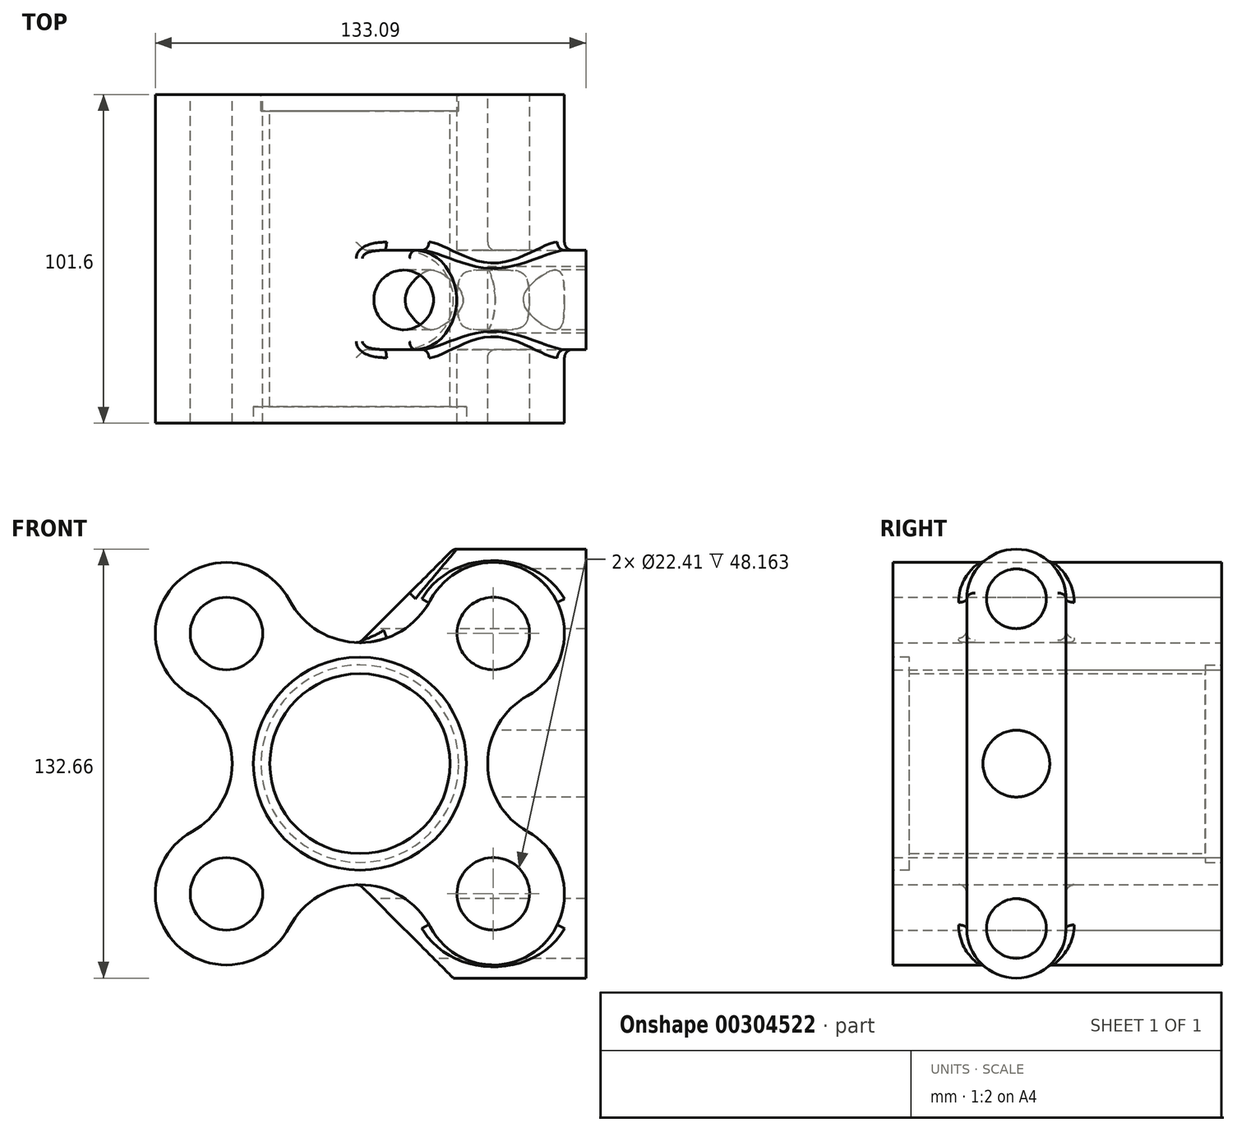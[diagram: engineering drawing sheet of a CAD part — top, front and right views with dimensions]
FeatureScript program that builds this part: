
annotation { "Feature Type Name" : "Feature", "Feature Type Description" : "" }
export const myFeature = defineFeature(function(context is Context, id is Id, definition is map)
    precondition{}
    {
        {
            var Q0;
            Q0=qCreatedBy(makeId("Front.planeOp"),FACE);
            var sketch = newSketch(context, id + "F0", { "sketchPlane" : qUnion([Q0])});
            skCircle(sketch, "E0", {"center": v(-41.24, 40.26) * mm, "radius": 11.2 * mm});
            skCircle(sketch, "E1.MirrorC", {"center": v(41.24, 40.26) * mm, "radius": 11.2 * mm});
            skCircle(sketch, "E2.MirrorC", {"center": v(-41.24, -40.26) * mm, "radius": 11.2 * mm});
            skCircle(sketch, "E3.MirrorC", {"center": v(41.24, -40.26) * mm, "radius": 11.2 * mm});
            skCircle(sketch, "E4", {"center": v(0, 0) * mm, "radius": 27.83 * mm});
            skArc(sketch, "E5", {"start": v(-21.8, 50.56) * mm, "mid": v(-56.66, 55.95) * mm, "end": v(-51.88, 21.01) * mm});
            skArc(sketch, "E6.MirrorC", {"start": v(-21.8, -50.56) * mm, "mid": v(-56.66, -55.95) * mm, "end": v(-51.88, -21.01) * mm});
            skArc(sketch, "E7.MirrorC", {"start": v(21.8, 50.56) * mm, "mid": v(56.66, 55.95) * mm, "end": v(51.88, 21.01) * mm});
            skArc(sketch, "E8.MirrorC", {"start": v(21.8, -50.56) * mm, "mid": v(56.66, -55.95) * mm, "end": v(51.88, -21.01) * mm});
            skArc(sketch, "E9", {"start": v(-51.88, -21.01) * mm, "mid": v(-39.5, 0) * mm, "end": v(-51.88, 21.01) * mm});
            skArc(sketch, "E10.MirrorC", {"start": v(51.88, -21.01) * mm, "mid": v(39.5, 0) * mm, "end": v(51.88, 21.01) * mm});
            skArc(sketch, "E11", {"start": v(-21.8, 50.56) * mm, "mid": v(0, 37.44) * mm, "end": v(21.8, 50.56) * mm});
            skArc(sketch, "E12.MirrorC", {"start": v(-21.8, -50.56) * mm, "mid": v(0, -37.44) * mm, "end": v(21.8, -50.56) * mm});
            skCircle(sketch, "E13", {"center": v(0, 0) * mm, "radius": 21.8 * mm});
            skPoint(sketch, "E14", {"position": v(0, 37.44) * mm});
            skSolve(sketch);
        }
        {
            var Q0;
            Q0=qCreatedBy(makeId("Right.planeOp"),FACE);
            var sketch = newSketch(context, id + "F1", { "sketchPlane" : qUnion([Q0])});
            skLineSegment(sketch, "E15.bottom", {"start": v(-15.34, 51) * mm, "end": v(15.34, 51) * mm});
            skLineSegment(sketch, "E15.top", {"start": v(-15.34, -51) * mm, "end": v(15.34, -51) * mm});
            skLineSegment(sketch, "E15.left", {"start": v(-15.34, 51) * mm, "end": v(-15.34, -51) * mm});
            skLineSegment(sketch, "E15.right", {"start": v(15.34, 51) * mm, "end": v(15.34, -51) * mm});
            skPoint(sketch, "E15.middle", {"position": v(0, 0) * mm});
            skArc(sketch, "E16", {"start": v(15.34, 51) * mm, "mid": v(0, 66.33) * mm, "end": v(-15.34, 51) * mm});
            skArc(sketch, "E17.MirrorCS", {"start": v(15.34, -51) * mm, "mid": v(0, -66.33) * mm, "end": v(-15.34, -51) * mm});
            skCircle(sketch, "E18", {"center": v(0, 51) * mm, "radius": 9.23 * mm});
            skCircle(sketch, "E19", {"center": v(0, 0) * mm, "radius": 10.32 * mm});
            skCircle(sketch, "E20.MirrorC", {"center": v(0, -51) * mm, "radius": 9.23 * mm});
            skSolve(sketch);
        }
        {
            var Q0;
            Q0=makeQuery(id+"F0.imprint","IMPRINT",FACE,{"disambiguationData":[TD([[makeQuery(id+"F0.imprint","IMPRINT",EDGE,{"derivedFrom":sQuery(id+"F0.wireOp",EDGE,"E0")}),-1.0]])]});
            extrude(context, id + "F2", {"entities" : qUnion([Q0]), "endBound" : BoundingType.SYMMETRIC, "depth" : 76.2 * mm});
        }
        {
            var Q0;
            Q0 = qSketchRegion(id + "F1", true);
            extrude(context, id + "F3", {"entities" : qUnion([Q0]), "operationType" : NewBodyOperationType.ADD, "depth" : 69.85 * mm});
        }
        {
            var Q0;
            Q0=makeQuery(id+"F2.opExtrude","CAP_FACE",FACE,{"disambiguationData":[OSD([sQuery(id+"F0.wireOp",EDGE,"E0"),sQuery(id+"F0.wireOp",EDGE,"E1.MirrorC"),sQuery(id+"F0.wireOp",EDGE,"E2.MirrorC"),sQuery(id+"F0.wireOp",EDGE,"E4"),sQuery(id+"F0.wireOp",EDGE,"E5"),sQuery(id+"F0.wireOp",EDGE,"E6.MirrorC"),sQuery(id+"F0.wireOp",EDGE,"E3.MirrorC"),sQuery(id+"F0.wireOp",EDGE,"E7.MirrorC"),sQuery(id+"F0.wireOp",EDGE,"E8.MirrorC"),sQuery(id+"F0.wireOp",EDGE,"E9"),sQuery(id+"F0.wireOp",EDGE,"E10.MirrorC"),sQuery(id+"F0.wireOp",EDGE,"E11"),sQuery(id+"F0.wireOp",EDGE,"E12.MirrorC")])],"isStart":false});
            var sketch = newSketch(context, id + "F4", { "sketchPlane" : qUnion([Q0])});
            skLineSegment(sketch, "E21.0", {"start": v(0, 51) * mm, "end": v(0, 66.33) * mm});
            skLineSegment(sketch, "E21.1", {"start": v(69.85, 51) * mm, "end": v(69.85, 66.33) * mm});
            skLineSegment(sketch, "E21.2", {"start": v(69.85, 51) * mm, "end": v(69.85, -51) * mm});
            skLineSegment(sketch, "E21.3", {"start": v(69.85, -51) * mm, "end": v(69.85, -66.33) * mm});
            skLineSegment(sketch, "E21.4", {"start": v(0, -51) * mm, "end": v(0, -66.33) * mm});
            skLineSegment(sketch, "E21.5", {"start": v(0, -37.44) * mm, "end": v(0, -51) * mm});
            skLineSegment(sketch, "E21.6", {"start": v(0, 51) * mm, "end": v(0, 37.44) * mm});
            skLineSegment(sketch, "E22", {"start": v(0, 66.33) * mm, "end": v(69.85, 66.33) * mm});
            skLineSegment(sketch, "E23", {"start": v(69.85, -66.33) * mm, "end": v(0, -66.33) * mm});
            skLineSegment(sketch, "E24", {"start": v(0, 37.44) * mm, "end": v(28.9, 66.33) * mm});
            skLineSegment(sketch, "E25", {"start": v(0, -37.44) * mm, "end": v(28.9, -66.33) * mm});
            skSolve(sketch);
        }
        {
            var Q0;
            Q0 = qSketchRegion(id + "F4", true);
            extrude(context, id + "F5", {"entities" : qUnion([Q0]), "operationType" : NewBodyOperationType.REMOVE, "endBound" : BoundingType.THROUGH_ALL, "oppositeDirection" : true, "depth" : 25.4 * mm});
        }
        {
            var Q0;
            {var subQ0=sQuery(id+"F1.wireOp",EDGE,"E15.left");Q0=makeQuery(id+"F3.boolean.opBoolean","SPLIT",FACE,{"disambiguationData":[TD([makeQuery(id+"F2.opExtrude","SWEPT_FACE",FACE,{"disambiguationData":[OSD([sQuery(id+"F0.wireOp",EDGE,"E4")])]})])],"derivedFrom":makeQuery(id+"F3.opExtrude","SWEPT_FACE",FACE,{"disambiguationData":[OSD([subQ0])]})});}
            extrude(context, id + "F6", {"entities" : qUnion([Q0]), "operationType" : NewBodyOperationType.REMOVE, "endBound" : BoundingType.THROUGH_ALL, "oppositeDirection" : true, "depth" : 25.4 * mm});
        }
        {
            var Q0;
            Q0=makeQuery(id+"F2.opExtrude","CAP_FACE",FACE,{"disambiguationData":[OSD([sQuery(id+"F0.wireOp",EDGE,"E0"),sQuery(id+"F0.wireOp",EDGE,"E1.MirrorC"),sQuery(id+"F0.wireOp",EDGE,"E2.MirrorC"),sQuery(id+"F0.wireOp",EDGE,"E4"),sQuery(id+"F0.wireOp",EDGE,"E5"),sQuery(id+"F0.wireOp",EDGE,"E6.MirrorC"),sQuery(id+"F0.wireOp",EDGE,"E3.MirrorC"),sQuery(id+"F0.wireOp",EDGE,"E7.MirrorC"),sQuery(id+"F0.wireOp",EDGE,"E8.MirrorC"),sQuery(id+"F0.wireOp",EDGE,"E9"),sQuery(id+"F0.wireOp",EDGE,"E10.MirrorC"),sQuery(id+"F0.wireOp",EDGE,"E11"),sQuery(id+"F0.wireOp",EDGE,"E12.MirrorC")])],"isStart":false});
            var sketch = newSketch(context, id + "F7", { "sketchPlane" : qUnion([Q0])});
            skCircle(sketch, "E26", {"center": v(0, 0) * mm, "radius": 32.92 * mm});
            skSolve(sketch);
        }
        {
            var Q0;
            Q0=makeQuery(id+"F7.imprint","IMPRINT",FACE,{"disambiguationData":[TD([[makeQuery(id+"F7.imprint","IMPRINT",EDGE,{"derivedFrom":sQuery(id+"F7.wireOp",EDGE,"E26")}),1.0]])]});
            var Q1;
            Q1=sQuery(id+"F7.wireOp",EDGE,"E26");
            extrude(context, id + "F8", {"entities" : qUnion([Q0]), "operationType" : NewBodyOperationType.REMOVE, "surfaceEntities" : qUnion([Q1]), "oppositeDirection" : true, "depth" : 5.08 * mm});
        }
        {
            var Q0;
            {var subQ1=sQuery(id+"F1.wireOp",EDGE,"E15.left");Q0=makeQuery(id+"F5.boolean.opBoolean","INTERSECT",EDGE,{"derivedFrom":[makeQuery(id+"F3.boolean.opBoolean","SPLIT",FACE,{"disambiguationData":[TD([makeQuery(id+"F2.opExtrude","SWEPT_FACE",FACE,{"disambiguationData":[OSD([sQuery(id+"F0.wireOp",EDGE,"E11")])]})])],"derivedFrom":makeQuery(id+"F3.opExtrude","SWEPT_FACE",FACE,{"disambiguationData":[OSD([subQ1])]})}),makeQuery(id+"F5.opExtrude","SWEPT_FACE",FACE,{"disambiguationData":[OSD([sQuery(id+"F4.wireOp",EDGE,"E24")])]})]});}
            var Q1;
            Q1=makeQuery(id+"F3.boolean.opBoolean","INTERSECT",EDGE,{"derivedFrom":[makeQuery(id+"F2.opExtrude","SWEPT_FACE",FACE,{"disambiguationData":[OSD([sQuery(id+"F0.wireOp",EDGE,"E11")])]}),makeQuery(id+"F3.opExtrude","SWEPT_FACE",FACE,{"disambiguationData":[OSD([sQuery(id+"F1.wireOp",EDGE,"E15.left")])]})]});
            var Q2;
            Q2=makeQuery(id+"F3.boolean.opBoolean","INTERSECT",EDGE,{"disambiguationData":[OD(1.0)],"derivedFrom":[makeQuery(id+"F2.opExtrude","SWEPT_FACE",FACE,{"disambiguationData":[OSD([sQuery(id+"F0.wireOp",EDGE,"E7.MirrorC")])]}),makeQuery(id+"F3.opExtrude","SWEPT_FACE",FACE,{"disambiguationData":[OSD([sQuery(id+"F1.wireOp",EDGE,"E16")])]})]});
            var Q3;
            {var subQ0=sQuery(id+"F0.wireOp",EDGE,"E11");Q3=makeQuery(id+"F5.boolean.opBoolean","MERGE",EDGE,{"derivedFrom":[makeQuery(id+"F3.boolean.opBoolean","INTERSECT",EDGE,{"derivedFrom":[makeQuery(id+"F2.opExtrude","SWEPT_FACE",FACE,{"disambiguationData":[OSD([subQ0])]}),makeQuery(id+"F3.opExtrude","CAP_FACE",FACE,{"disambiguationData":[OSD([sQuery(id+"F1.wireOp",EDGE,"E15.left"),sQuery(id+"F1.wireOp",EDGE,"E15.right"),sQuery(id+"F1.wireOp",EDGE,"E16"),sQuery(id+"F1.wireOp",EDGE,"E17.MirrorCS"),sQuery(id+"F1.wireOp",EDGE,"E18"),sQuery(id+"F1.wireOp",EDGE,"E19"),sQuery(id+"F1.wireOp",EDGE,"E20.MirrorC")])],"isStart":true})]}),makeQuery(id+"F5.opExtrude","SWEPT_EDGE",EDGE,{"disambiguationData":[OSD([subQ0,sQuery(id+"F4.wireOp",EDGE,"E21.6"),sQuery(id+"F4.wireOp",EDGE,"E24")])]})]});}
            fillet(context, id + "F9", {"entities" : qUnion([Q0, Q1, Q2, Q3]), "radius" : 2.54 * mm, "tangentPropagation" : true, "allowEdgeOverflow" : false});
        }
        {
            var Q0;
            {var subQ0=sQuery(id+"F0.wireOp",EDGE,"E12.MirrorC");Q0=makeQuery(id+"F5.boolean.opBoolean","MERGE",EDGE,{"derivedFrom":[makeQuery(id+"F3.boolean.opBoolean","INTERSECT",EDGE,{"derivedFrom":[makeQuery(id+"F2.opExtrude","SWEPT_FACE",FACE,{"disambiguationData":[OSD([subQ0])]}),makeQuery(id+"F3.opExtrude","CAP_FACE",FACE,{"disambiguationData":[OSD([sQuery(id+"F1.wireOp",EDGE,"E15.left"),sQuery(id+"F1.wireOp",EDGE,"E15.right"),sQuery(id+"F1.wireOp",EDGE,"E16"),sQuery(id+"F1.wireOp",EDGE,"E17.MirrorCS"),sQuery(id+"F1.wireOp",EDGE,"E18"),sQuery(id+"F1.wireOp",EDGE,"E19"),sQuery(id+"F1.wireOp",EDGE,"E20.MirrorC")])],"isStart":true})]}),makeQuery(id+"F5.opExtrude","SWEPT_EDGE",EDGE,{"disambiguationData":[OSD([subQ0,sQuery(id+"F4.wireOp",EDGE,"E21.5"),sQuery(id+"F4.wireOp",EDGE,"E25")])]})]});}
            fillet(context, id + "F10", {"entities" : qUnion([Q0]), "radius" : 2.54 * mm, "tangentPropagation" : true, "allowEdgeOverflow" : false});
        }
        {
            var Q0;
            Q0=makeQuery(id+"F2.opExtrude","CAP_FACE",FACE,{"disambiguationData":[OSD([sQuery(id+"F0.wireOp",EDGE,"E0"),sQuery(id+"F0.wireOp",EDGE,"E1.MirrorC"),sQuery(id+"F0.wireOp",EDGE,"E2.MirrorC"),sQuery(id+"F0.wireOp",EDGE,"E4"),sQuery(id+"F0.wireOp",EDGE,"E5"),sQuery(id+"F0.wireOp",EDGE,"E6.MirrorC"),sQuery(id+"F0.wireOp",EDGE,"E3.MirrorC"),sQuery(id+"F0.wireOp",EDGE,"E7.MirrorC"),sQuery(id+"F0.wireOp",EDGE,"E8.MirrorC"),sQuery(id+"F0.wireOp",EDGE,"E9"),sQuery(id+"F0.wireOp",EDGE,"E10.MirrorC"),sQuery(id+"F0.wireOp",EDGE,"E11"),sQuery(id+"F0.wireOp",EDGE,"E12.MirrorC")])],"isStart":true});
            extrude(context, id + "F11", {"entities" : qUnion([Q0]), "operationType" : NewBodyOperationType.ADD, "depth" : 25.4 * mm});
        }
        {
            var Q0;
            Q0=makeQuery(id+"F11.opExtrude","CAP_FACE",FACE,{"disambiguationData":[OSD([sQuery(id+"F0.wireOp",EDGE,"E0"),sQuery(id+"F0.wireOp",EDGE,"E1.MirrorC"),sQuery(id+"F0.wireOp",EDGE,"E2.MirrorC"),sQuery(id+"F0.wireOp",EDGE,"E4"),sQuery(id+"F0.wireOp",EDGE,"E5"),sQuery(id+"F0.wireOp",EDGE,"E6.MirrorC"),sQuery(id+"F0.wireOp",EDGE,"E3.MirrorC"),sQuery(id+"F0.wireOp",EDGE,"E7.MirrorC"),sQuery(id+"F0.wireOp",EDGE,"E8.MirrorC"),sQuery(id+"F0.wireOp",EDGE,"E9"),sQuery(id+"F0.wireOp",EDGE,"E10.MirrorC"),sQuery(id+"F0.wireOp",EDGE,"E11"),sQuery(id+"F0.wireOp",EDGE,"E12.MirrorC")])],"isStart":false});
            var sketch = newSketch(context, id + "F12", { "sketchPlane" : qUnion([Q0])});
            skCircle(sketch, "E27", {"center": v(0, 0) * mm, "radius": 30.55 * mm});
            skSolve(sketch);
        }
        {
            var Q0;
            Q0=makeQuery(id+"F12.imprint","IMPRINT",FACE,{"disambiguationData":[TD([[makeQuery(id+"F12.imprint","IMPRINT",EDGE,{"derivedFrom":sQuery(id+"F12.wireOp",EDGE,"E27")}),1.0]])]});
            extrude(context, id + "F13", {"entities" : qUnion([Q0]), "operationType" : NewBodyOperationType.REMOVE, "oppositeDirection" : true, "depth" : 5.08 * mm});
        }
    });
